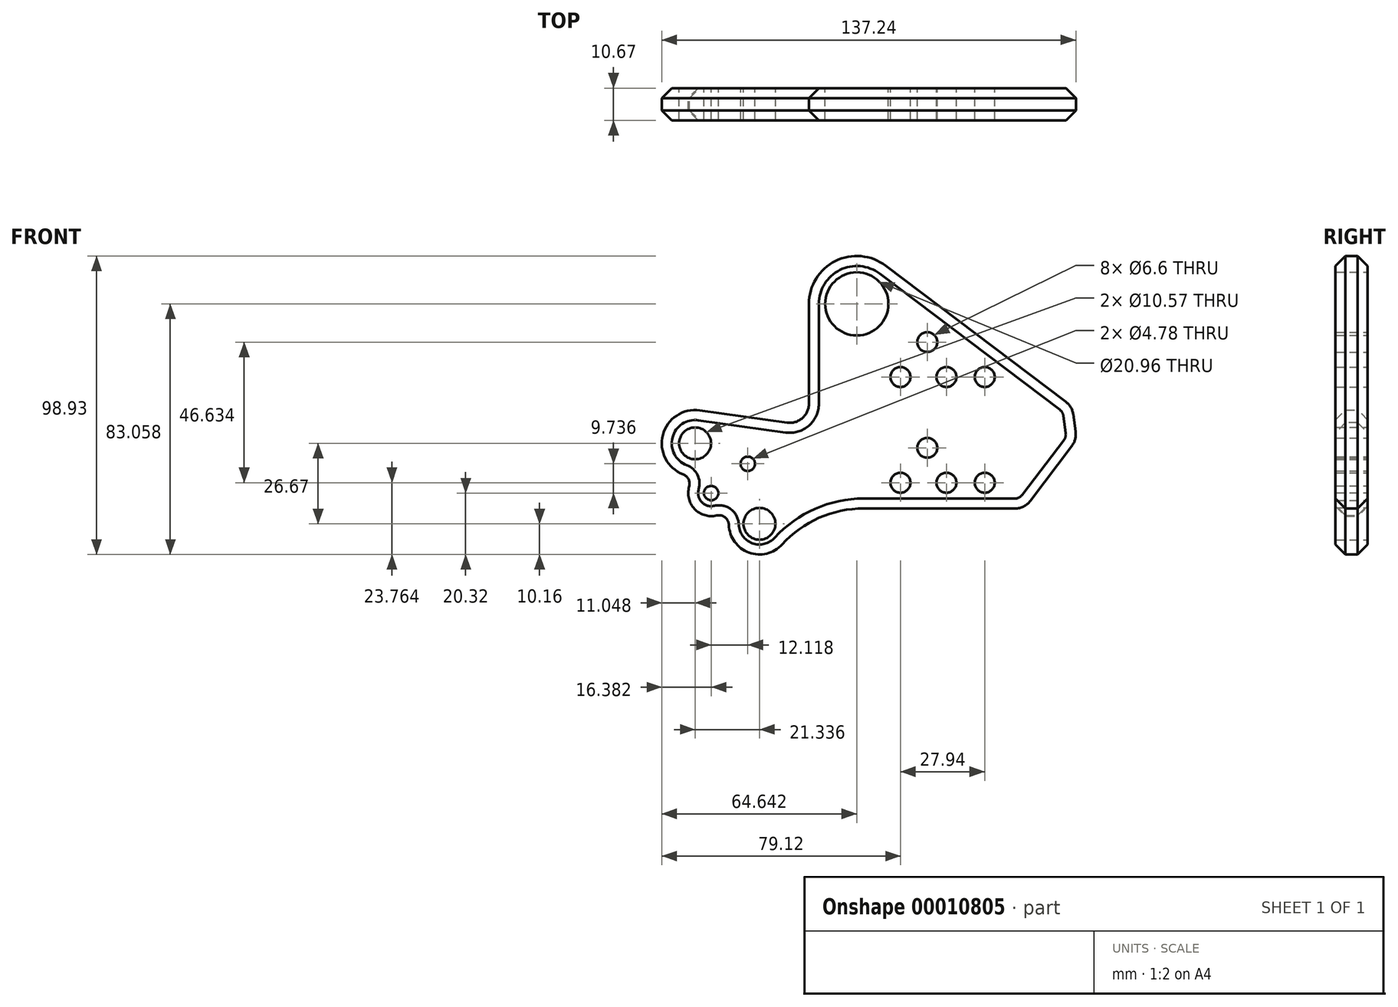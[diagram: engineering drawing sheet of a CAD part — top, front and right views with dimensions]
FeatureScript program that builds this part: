
annotation { "Feature Type Name" : "Feature", "Feature Type Description" : "" }
export const myFeature = defineFeature(function(context is Context, id is Id, definition is map)
    precondition{}
    {
        {
            var Q0;
            Q0=qCreatedBy(makeId("Front.planeOp"),FACE);
            var sketch = newSketch(context, id + "F0", { "sketchPlane" : qUnion([Q0])});
            skLineSegment(sketch, "E0", {"start": v(-17.27, 0) * mm, "end": v(0, 22.86) * mm});
            skLineSegment(sketch, "E1", {"start": v(0, 22.86) * mm, "end": v(-1.52, 33.78) * mm});
            skLineSegment(sketch, "E2", {"start": v(-1.52, 33.78) * mm, "end": v(-63.33, 80.48) * mm});
            skLineSegment(sketch, "E3", {"start": v(-88.77, 67.82) * mm, "end": v(-88.77, 27.43) * mm});
            skLineSegment(sketch, "E4", {"start": v(-88.77, 27.43) * mm, "end": v(-124.95, 32.53) * mm});
            skLineSegment(sketch, "E5", {"start": v(-17.27, 0) * mm, "end": v(-70.61, 0) * mm});
            skArc(sketch, "E6", {"start": v(-70.61, 0) * mm, "mid": v(-85.39, -3.11) * mm, "end": v(-97.65, -11.93) * mm});
            skArc(sketch, "E7", {"start": v(-63.33, 80.48) * mm, "mid": v(-79.97, 82.03) * mm, "end": v(-88.77, 67.82) * mm});
            skArc(sketch, "E8", {"start": v(-124.95, 32.53) * mm, "mid": v(-137.19, 24.36) * mm, "end": v(-130.45, 11.27) * mm});
            skArc(sketch, "E9", {"start": v(-128.46, 7.25) * mm, "mid": v(-128.67, 9.65) * mm, "end": v(-130.45, 11.27) * mm});
            skArc(sketch, "E10", {"start": v(-128.46, 7.25) * mm, "mid": v(-126.69, -0.16) * mm, "end": v(-119.38, -2.33) * mm});
            skArc(sketch, "E11", {"start": v(-115.31, -5.43) * mm, "mid": v(-116.61, -2.91) * mm, "end": v(-119.38, -2.33) * mm});
            skArc(sketch, "E12", {"start": v(-115.31, -5.43) * mm, "mid": v(-108.67, -14.61) * mm, "end": v(-97.65, -11.93) * mm});
            skSolve(sketch);
        }
        {
            var Q0;
            Q0=makeQuery(id+"F0.imprint","IMPRINT",FACE,{"disambiguationData":[TD([[makeQuery(id+"F0.imprint","IMPRINT",EDGE,{"derivedFrom":sQuery(id+"F0.wireOp",EDGE,"E0")}),1.0]])]});
            extrude(context, id + "F1", {"entities" : qUnion([Q0]), "depth" : 10.67 * mm});
        }
        {
            var Q0;
            Q0=makeQuery(id+"F1.opExtrude","SWEPT_EDGE",EDGE,{"disambiguationData":[OSD([sQuery(id+"F0.wireOp",EDGE,"E0"),sQuery(id+"F0.wireOp",EDGE,"E5")])]});
            var Q1;
            Q1=makeQuery(id+"F1.opExtrude","SWEPT_EDGE",EDGE,{"disambiguationData":[OSD([sQuery(id+"F0.wireOp",EDGE,"E0"),sQuery(id+"F0.wireOp",EDGE,"E1")])]});
            var Q2;
            Q2=makeQuery(id+"F1.opExtrude","SWEPT_EDGE",EDGE,{"disambiguationData":[OSD([sQuery(id+"F0.wireOp",EDGE,"E1"),sQuery(id+"F0.wireOp",EDGE,"E2")])]});
            var Q3;
            Q3=makeQuery(id+"F1.opExtrude","SWEPT_EDGE",EDGE,{"disambiguationData":[OSD([sQuery(id+"F0.wireOp",EDGE,"E3"),sQuery(id+"F0.wireOp",EDGE,"E4")])]});
            fillet(context, id + "F2", {"entities" : qUnion([Q0, Q1, Q2, Q3]), "radius" : 6.35 * mm, "tangentPropagation" : true, "allowEdgeOverflow" : false});
        }
        {
            var Q0;
            Q0=qCreatedBy(makeId("Front.planeOp"),FACE);
            var sketch = newSketch(context, id + "F3", { "sketchPlane" : qUnion([Q0])});
            skCircle(sketch, "E13", {"center": v(-72.9, 67.82) * mm, "radius": 10.48 * mm});
            skSolve(sketch);
        }
        {
            var Q0;
            Q0=makeQuery(id+"F3.imprint","IMPRINT",FACE,{"disambiguationData":[TD([[makeQuery(id+"F3.imprint","IMPRINT",EDGE,{"derivedFrom":sQuery(id+"F3.wireOp",EDGE,"E13")}),1.0]])]});
            extrude(context, id + "F4", {"entities" : qUnion([Q0]), "operationType" : NewBodyOperationType.REMOVE, "endBound" : BoundingType.THROUGH_ALL, "depth" : 25.4 * mm});
        }
        {
            var Q0;
            Q0=qCreatedBy(makeId("Front.planeOp"),FACE);
            var sketch = newSketch(context, id + "F5", { "sketchPlane" : qUnion([Q0])});
            skCircle(sketch, "E14", {"center": v(-30.48, 8.52) * mm, "radius": 3.3 * mm});
            skCircle(sketch, "E15", {"center": v(-30.48, 43.58) * mm, "radius": 3.3 * mm});
            skCircle(sketch, "E16", {"center": v(-43.18, 8.52) * mm, "radius": 3.3 * mm});
            skCircle(sketch, "E17", {"center": v(-58.42, 8.52) * mm, "radius": 3.3 * mm});
            skCircle(sketch, "E18", {"center": v(-49.53, 20.1) * mm, "radius": 3.3 * mm});
            skCircle(sketch, "E19", {"center": v(-43.18, 43.58) * mm, "radius": 3.3 * mm});
            skCircle(sketch, "E20", {"center": v(-58.42, 43.58) * mm, "radius": 3.3 * mm});
            skCircle(sketch, "E21", {"center": v(-49.53, 55.16) * mm, "radius": 3.3 * mm});
            skSolve(sketch);
        }
        {
            var Q0;
            Q0=makeQuery(id+"F5.imprint","IMPRINT",FACE,{"disambiguationData":[TD([[makeQuery(id+"F5.imprint","IMPRINT",EDGE,{"derivedFrom":sQuery(id+"F5.wireOp",EDGE,"E21")}),1.0]])]});
            var Q1;
            Q1=makeQuery(id+"F5.imprint","IMPRINT",FACE,{"disambiguationData":[TD([[makeQuery(id+"F5.imprint","IMPRINT",EDGE,{"derivedFrom":sQuery(id+"F5.wireOp",EDGE,"E20")}),1.0]])]});
            var Q2;
            Q2=makeQuery(id+"F5.imprint","IMPRINT",FACE,{"disambiguationData":[TD([[makeQuery(id+"F5.imprint","IMPRINT",EDGE,{"derivedFrom":sQuery(id+"F5.wireOp",EDGE,"E19")}),1.0]])]});
            var Q3;
            Q3=makeQuery(id+"F5.imprint","IMPRINT",FACE,{"disambiguationData":[TD([[makeQuery(id+"F5.imprint","IMPRINT",EDGE,{"derivedFrom":sQuery(id+"F5.wireOp",EDGE,"E15")}),1.0]])]});
            var Q4;
            Q4=makeQuery(id+"F5.imprint","IMPRINT",FACE,{"disambiguationData":[TD([[makeQuery(id+"F5.imprint","IMPRINT",EDGE,{"derivedFrom":sQuery(id+"F5.wireOp",EDGE,"E18")}),1.0]])]});
            var Q5;
            Q5=makeQuery(id+"F5.imprint","IMPRINT",FACE,{"disambiguationData":[TD([[makeQuery(id+"F5.imprint","IMPRINT",EDGE,{"derivedFrom":sQuery(id+"F5.wireOp",EDGE,"E17")}),1.0]])]});
            var Q6;
            Q6=makeQuery(id+"F5.imprint","IMPRINT",FACE,{"disambiguationData":[TD([[makeQuery(id+"F5.imprint","IMPRINT",EDGE,{"derivedFrom":sQuery(id+"F5.wireOp",EDGE,"E16")}),1.0]])]});
            var Q7;
            Q7=makeQuery(id+"F5.imprint","IMPRINT",FACE,{"disambiguationData":[TD([[makeQuery(id+"F5.imprint","IMPRINT",EDGE,{"derivedFrom":sQuery(id+"F5.wireOp",EDGE,"E14")}),1.0]])]});
            extrude(context, id + "F6", {"entities" : qUnion([Q0, Q1, Q2, Q3, Q4, Q5, Q6, Q7]), "operationType" : NewBodyOperationType.REMOVE, "endBound" : BoundingType.THROUGH_ALL, "depth" : 25.4 * mm});
        }
        {
            var Q0;
            Q0=qCreatedBy(makeId("Front.planeOp"),FACE);
            var sketch = newSketch(context, id + "F7", { "sketchPlane" : qUnion([Q0])});
            skCircle(sketch, "E22", {"center": v(-126.5, 21.59) * mm, "radius": 5.28 * mm});
            skCircle(sketch, "E23", {"center": v(-105.16, -5.08) * mm, "radius": 5.28 * mm});
            skSolve(sketch);
        }
        {
            var Q0;
            Q0=makeQuery(id+"F7.imprint","IMPRINT",FACE,{"disambiguationData":[TD([[makeQuery(id+"F7.imprint","IMPRINT",EDGE,{"derivedFrom":sQuery(id+"F7.wireOp",EDGE,"E22")}),1.0]])]});
            var Q1;
            Q1=makeQuery(id+"F7.imprint","IMPRINT",FACE,{"disambiguationData":[TD([[makeQuery(id+"F7.imprint","IMPRINT",EDGE,{"derivedFrom":sQuery(id+"F7.wireOp",EDGE,"E23")}),1.0]])]});
            extrude(context, id + "F8", {"entities" : qUnion([Q0, Q1]), "operationType" : NewBodyOperationType.REMOVE, "endBound" : BoundingType.THROUGH_ALL, "depth" : 25.4 * mm});
        }
        {
            var Q0;
            Q0=qCreatedBy(makeId("Front.planeOp"),FACE);
            var sketch = newSketch(context, id + "F9", { "sketchPlane" : qUnion([Q0])});
            skCircle(sketch, "E24", {"center": v(-121.16, 5.08) * mm, "radius": 2.39 * mm});
            skCircle(sketch, "E25", {"center": v(-109.04, 14.82) * mm, "radius": 2.39 * mm});
            skLineSegment(sketch, "E26", {"start": v(-130.53, 18.18) * mm, "end": v(-108.66, -9.03) * mm, "construction": true});
            skLineSegment(sketch, "E27", {"start": v(-121.16, 5.08) * mm, "end": v(-109.04, 14.82) * mm, "construction": true});
            skSolve(sketch);
        }
        {
            var Q0;
            Q0=makeQuery(id+"F9.imprint","IMPRINT",FACE,{"disambiguationData":[TD([[makeQuery(id+"F9.imprint","IMPRINT",EDGE,{"derivedFrom":sQuery(id+"F9.wireOp",EDGE,"E25")}),1.0]])]});
            var Q1;
            Q1=makeQuery(id+"F9.imprint","IMPRINT",FACE,{"disambiguationData":[TD([[makeQuery(id+"F9.imprint","IMPRINT",EDGE,{"derivedFrom":sQuery(id+"F9.wireOp",EDGE,"E24")}),1.0]])]});
            extrude(context, id + "F10", {"entities" : qUnion([Q0, Q1]), "operationType" : NewBodyOperationType.REMOVE, "endBound" : BoundingType.THROUGH_ALL, "depth" : 25.4 * mm});
        }
        {
            var Q0;
            Q0=makeQuery(id+"F1.opExtrude","CAP_EDGE",EDGE,{"disambiguationData":[OSD([sQuery(id+"F0.wireOp",EDGE,"E2")])],"isStart":false});
            var Q1;
            Q1=makeQuery(id+"F1.opExtrude","CAP_EDGE",EDGE,{"disambiguationData":[OSD([sQuery(id+"F0.wireOp",EDGE,"E2")])],"isStart":true});
            chamfer(context, id + "F11", {"entities" : qUnion([Q0, Q1]), "width" : 3.3 * mm, "tangentPropagation" : true});
        }
    });
